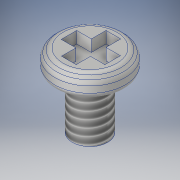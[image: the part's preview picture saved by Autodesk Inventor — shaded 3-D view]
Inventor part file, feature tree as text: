
AUTODESK INVENTOR PART (.ipt)
format: ipt  version: 2018 (Build 220112000, 112)  size: 171,008 bytes
history: native  units: in
note: dims shown in document units (in); Inventor stores cm internally (conversion verified against a paired STEP export)
features: sketch x2, revolve x1, chamfer x1, fillet x1, thread x1, extrude x1
ambient origin geometry x8: Origin, YZ Plane, XZ Plane, XY Plane, X Axis, Y Axis, Z Axis, Center Point
bodies: Solid1 (feature_tree)
feature tree (7):
  revolve  "Revolution1"  [1 undecoded]
  chamfer  "Chamfer1"  Distance=0.225in
  fillet  "Fillet1"  [1 undecoded]
  thread  "Thread1"  [1 undecoded]
  extrude  "Extrusion1"  Depth=0.025in TaperAngle=45.0deg
  sketch  "Sketch1"  dims[d0=0.15in d1=0.0875in]
  sketch  "Sketch2"  dims[d2=0.075in d3=0.225in d4=90.0deg d5=90.0deg d6=0.025in d7=0.125in d8=45.0deg d9=0.025in d10=1.0in d11=0.0in d12=0.05in d13=0.0in]
note: 3 required parameter values undecoded (feature->parameter linkage not recoverable at this tier; creation-order binding heuristic only, values carry confidence <= 0.55)